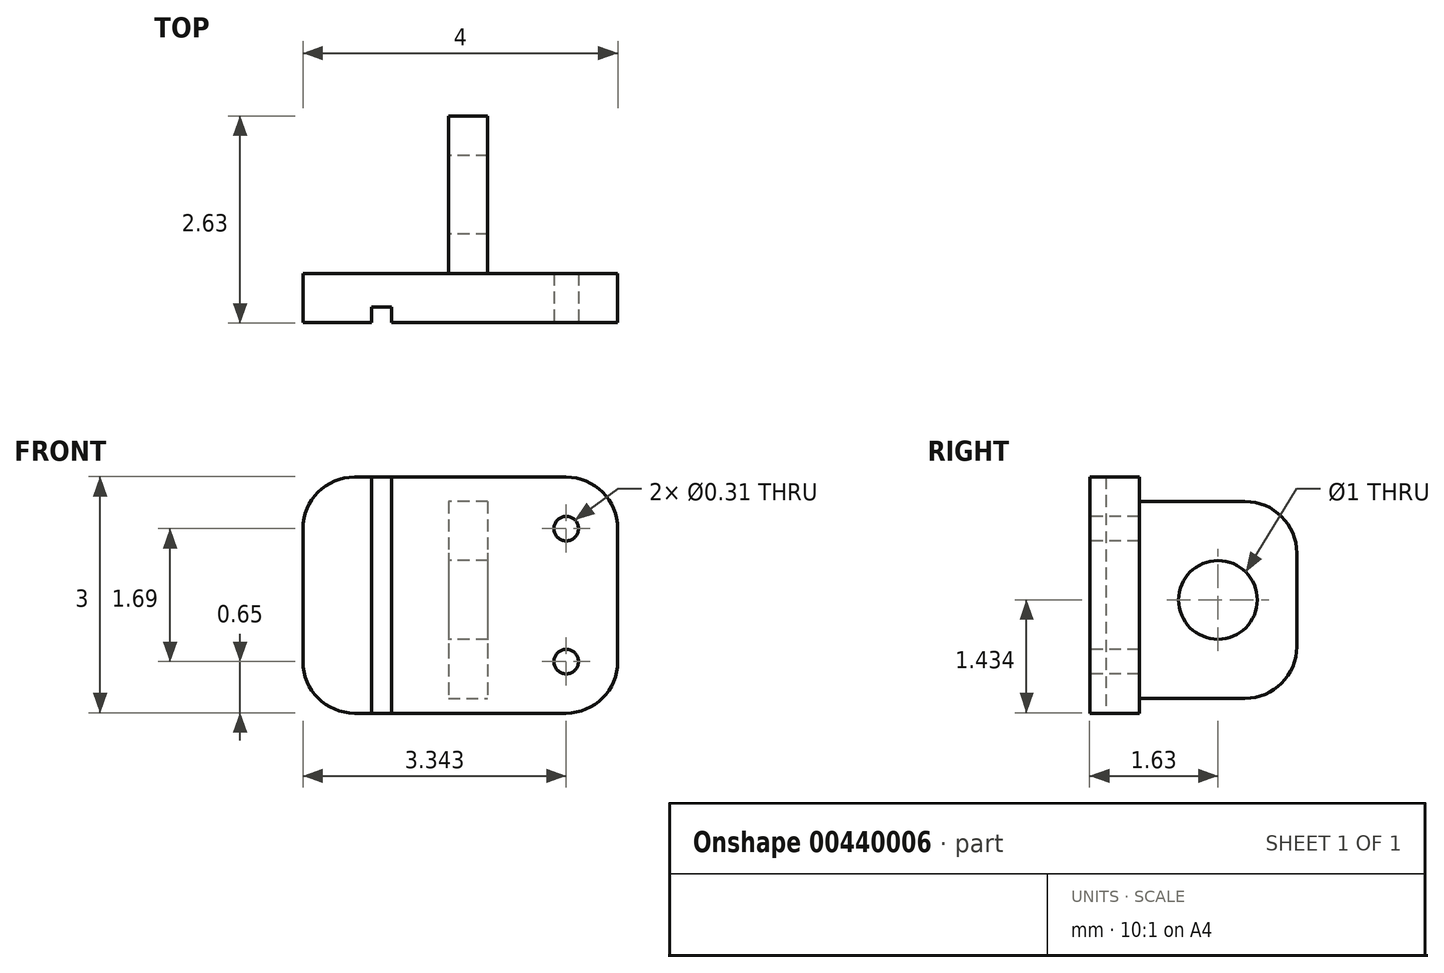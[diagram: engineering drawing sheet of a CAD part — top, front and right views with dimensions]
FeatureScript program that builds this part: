
annotation { "Feature Type Name" : "Feature", "Feature Type Description" : "" }
export const myFeature = defineFeature(function(context is Context, id is Id, definition is map)
    precondition{}
    {
        {
            var Q0;
            Q0=qCreatedBy(makeId("Front.planeOp"),FACE);
            var sketch = newSketch(context, id + "F0", { "sketchPlane" : qUnion([Q0])});
            skLineSegment(sketch, "E0", {"start": v(-11.13, 20.44) * mm, "end": v(-7.13, 20.44) * mm});
            skLineSegment(sketch, "E1", {"start": v(-7.13, 20.44) * mm, "end": v(-7.13, 17.44) * mm});
            skLineSegment(sketch, "E2", {"start": v(-7.13, 17.44) * mm, "end": v(-11.13, 17.44) * mm});
            skLineSegment(sketch, "E3", {"start": v(-11.13, 17.44) * mm, "end": v(-11.13, 20.44) * mm});
            skSolve(sketch);
        }
        {
            var Q0;
            Q0 = qSketchRegion(id + "F0", true);
            extrude(context, id + "F1", {"entities" : qUnion([Q0]), "depth" : .625 * mm});
        }
        {
            var Q0;
            Q0=makeQuery(id+"F1.opExtrude","SWEPT_EDGE",EDGE,{"disambiguationData":[OSD([sQuery(id+"F0.wireOp",EDGE,"E2"),sQuery(id+"F0.wireOp",EDGE,"E3")])]});
            var Q1;
            Q1=makeQuery(id+"F1.opExtrude","SWEPT_EDGE",EDGE,{"disambiguationData":[OSD([sQuery(id+"F0.wireOp",EDGE,"E1"),sQuery(id+"F0.wireOp",EDGE,"E2")])]});
            var Q2;
            Q2=makeQuery(id+"F1.opExtrude","SWEPT_EDGE",EDGE,{"disambiguationData":[OSD([sQuery(id+"F0.wireOp",EDGE,"E0"),sQuery(id+"F0.wireOp",EDGE,"E1")])]});
            var Q3;
            Q3=makeQuery(id+"F1.opExtrude","SWEPT_EDGE",EDGE,{"disambiguationData":[OSD([sQuery(id+"F0.wireOp",EDGE,"E0"),sQuery(id+"F0.wireOp",EDGE,"E3")])]});
            fillet(context, id + "F2", {"entities" : qUnion([Q0, Q1, Q2, Q3]), "radius" : .655 * mm, "tangentPropagation" : true, "allowEdgeOverflow" : false});
        }
        {
            var Q0;
            Q0=makeQuery(id+"F1.opExtrude","CAP_FACE",FACE,{"disambiguationData":[OSD([sQuery(id+"F0.wireOp",EDGE,"E0"),sQuery(id+"F0.wireOp",EDGE,"E1"),sQuery(id+"F0.wireOp",EDGE,"E2"),sQuery(id+"F0.wireOp",EDGE,"E3")])],"isStart":false});
            var sketch = newSketch(context, id + "F3", { "sketchPlane" : qUnion([Q0])});
            skLineSegment(sketch, "E4", {"start": v(-10.26, 20.44) * mm, "end": v(-10.26, 17.44) * mm});
            skLineSegment(sketch, "E5", {"start": v(-10.26, 20.44) * mm, "end": v(-10, 20.44) * mm});
            skLineSegment(sketch, "E6", {"start": v(-10, 20.44) * mm, "end": v(-10, 17.44) * mm});
            skLineSegment(sketch, "E7", {"start": v(-10, 17.44) * mm, "end": v(-10.26, 17.44) * mm});
            skSolve(sketch);
        }
        {
            var Q0;
            Q0 = qSketchRegion(id + "F3", true);
            extrude(context, id + "F4", {"entities" : qUnion([Q0]), "operationType" : NewBodyOperationType.REMOVE, "oppositeDirection" : true, "depth" : .200 * mm});
        }
        {
            var Q0;
            {var subQ0=sQuery(id+"F0.wireOp",EDGE,"E1");var subQ1=sQuery(id+"F0.wireOp",EDGE,"E0");var subQ2=sQuery(id+"F0.wireOp",EDGE,"E2");Q0=makeQuery(id+"F4.boolean.opBoolean","SPLIT",FACE,{"disambiguationData":[TD([makeQuery(id+"F1.opExtrude","SWEPT_FACE",FACE,{"disambiguationData":[OSD([subQ0])]})])],"derivedFrom":makeQuery(id+"F1.opExtrude","CAP_FACE",FACE,{"disambiguationData":[OSD([subQ1,subQ0,subQ2,sQuery(id+"F0.wireOp",EDGE,"E3")])],"isStart":false})});}
            var sketch = newSketch(context, id + "F5", { "sketchPlane" : qUnion([Q0])});
            skCircle(sketch, "E8", {"center": v(-7.79, 19.78) * mm, "radius": 0.16 * mm});
            skCircle(sketch, "E9", {"center": v(-7.79, 18.1) * mm, "radius": 0.16 * mm});
            skSolve(sketch);
        }
        {
            var Q0;
            Q0 = qSketchRegion(id + "F5", true);
            extrude(context, id + "F6", {"entities" : qUnion([Q0]), "operationType" : NewBodyOperationType.REMOVE, "oppositeDirection" : true, "depth" : 25 * mm});
        }
        {
            var Q0;
            Q0=makeQuery(id+"F1.opExtrude","CAP_FACE",FACE,{"disambiguationData":[OSD([sQuery(id+"F0.wireOp",EDGE,"E0"),sQuery(id+"F0.wireOp",EDGE,"E1"),sQuery(id+"F0.wireOp",EDGE,"E2"),sQuery(id+"F0.wireOp",EDGE,"E3")])],"isStart":true});
            var sketch = newSketch(context, id + "F7", { "sketchPlane" : qUnion([Q0])});
            skLineSegment(sketch, "E10", {"start": v(8.78, 20.12) * mm, "end": v(9.28, 20.12) * mm});
            skLineSegment(sketch, "E11", {"start": v(9.28, 20.12) * mm, "end": v(9.28, 17.62) * mm});
            skLineSegment(sketch, "E12", {"start": v(9.28, 17.62) * mm, "end": v(8.78, 17.62) * mm});
            skLineSegment(sketch, "E13", {"start": v(8.78, 20.12) * mm, "end": v(8.78, 17.62) * mm});
            skSolve(sketch);
        }
        {
            var Q0;
            Q0 = qSketchRegion(id + "F7", true);
            extrude(context, id + "F8", {"entities" : qUnion([Q0]), "operationType" : NewBodyOperationType.ADD, "depth" : 2 * mm});
        }
        {
            var Q0;
            Q0=makeQuery(id+"F8.opExtrude","SWEPT_FACE",FACE,{"disambiguationData":[OSD([sQuery(id+"F7.wireOp",EDGE,"E11")])]});
            var sketch = newSketch(context, id + "F9", { "sketchPlane" : qUnion([Q0])});
            skCircle(sketch, "E14", {"center": v(-1, 18.87) * mm, "radius": 0.5 * mm});
            skSolve(sketch);
        }
        {
            var Q0;
            Q0 = qSketchRegion(id + "F9", true);
            extrude(context, id + "F10", {"entities" : qUnion([Q0]), "operationType" : NewBodyOperationType.REMOVE, "oppositeDirection" : true, "depth" : 25 * mm});
        }
        {
            var Q0;
            Q0=makeQuery(id+"F8.opExtrude","CAP_EDGE",EDGE,{"disambiguationData":[OSD([sQuery(id+"F7.wireOp",EDGE,"E12")])],"isStart":false});
            fillet(context, id + "F11", {"entities" : qUnion([Q0]), "radius" : .655 * mm, "tangentPropagation" : true, "allowEdgeOverflow" : false});
        }
        {
            var Q0;
            Q0=makeQuery(id+"F8.opExtrude","CAP_EDGE",EDGE,{"disambiguationData":[OSD([sQuery(id+"F7.wireOp",EDGE,"E10")])],"isStart":false});
            fillet(context, id + "F12", {"entities" : qUnion([Q0]), "radius" : .655 * mm, "tangentPropagation" : true, "allowEdgeOverflow" : false});
        }
    });
